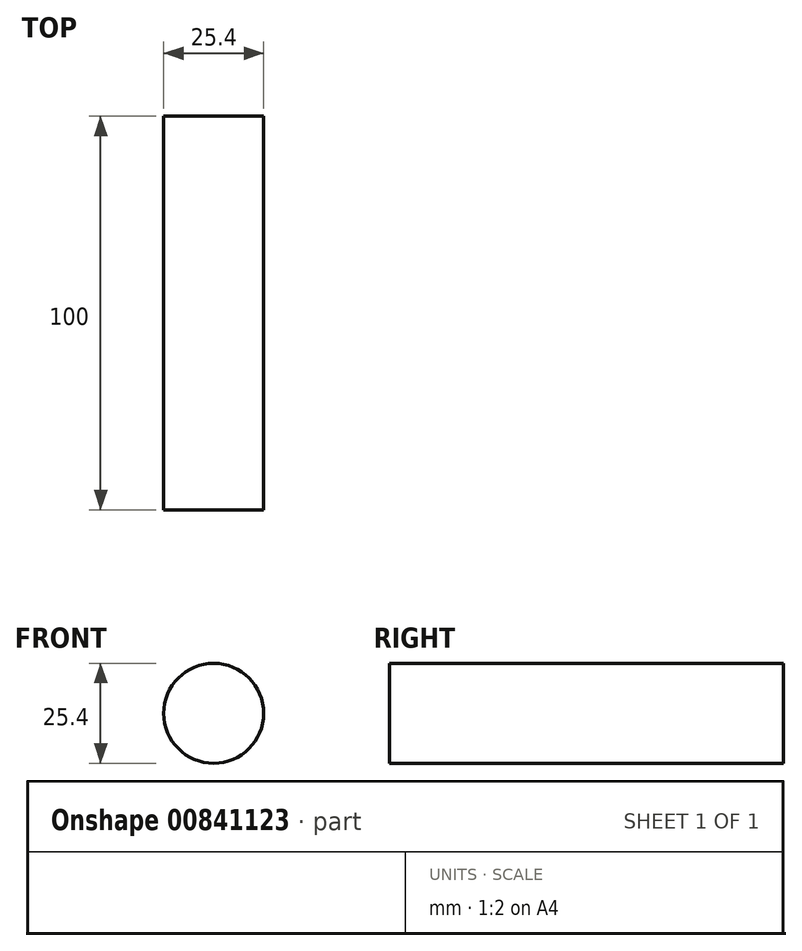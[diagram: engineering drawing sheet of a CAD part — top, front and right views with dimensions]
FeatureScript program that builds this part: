
annotation { "Feature Type Name" : "Feature", "Feature Type Description" : "" }
export const myFeature = defineFeature(function(context is Context, id is Id, definition is map)
    precondition{}
    {
        {
            var Q0;
            Q0=qCreatedBy(makeId("Front.planeOp"),FACE);
            var sketch = newSketch(context, id + "F0", { "sketchPlane" : qUnion([Q0])});
            skCircle(sketch, "E0", {"center": v(0, 0) * mm, "radius": 12.7 * mm});
            skSolve(sketch);
        }
        {
            var Q0;
            Q0=makeQuery(id+"F0.imprint","IMPRINT",FACE,{"disambiguationData":[TD([[makeQuery(id+"F0.imprint","IMPRINT",EDGE,{"derivedFrom":sQuery(id+"F0.wireOp",EDGE,"E0")}),1.0]])]});
            extrude(context, id + "F1", {"entities" : qUnion([Q0]), "depth" : 100 * mm, "offsetDistance" : 25 * mm});
        }
    });
